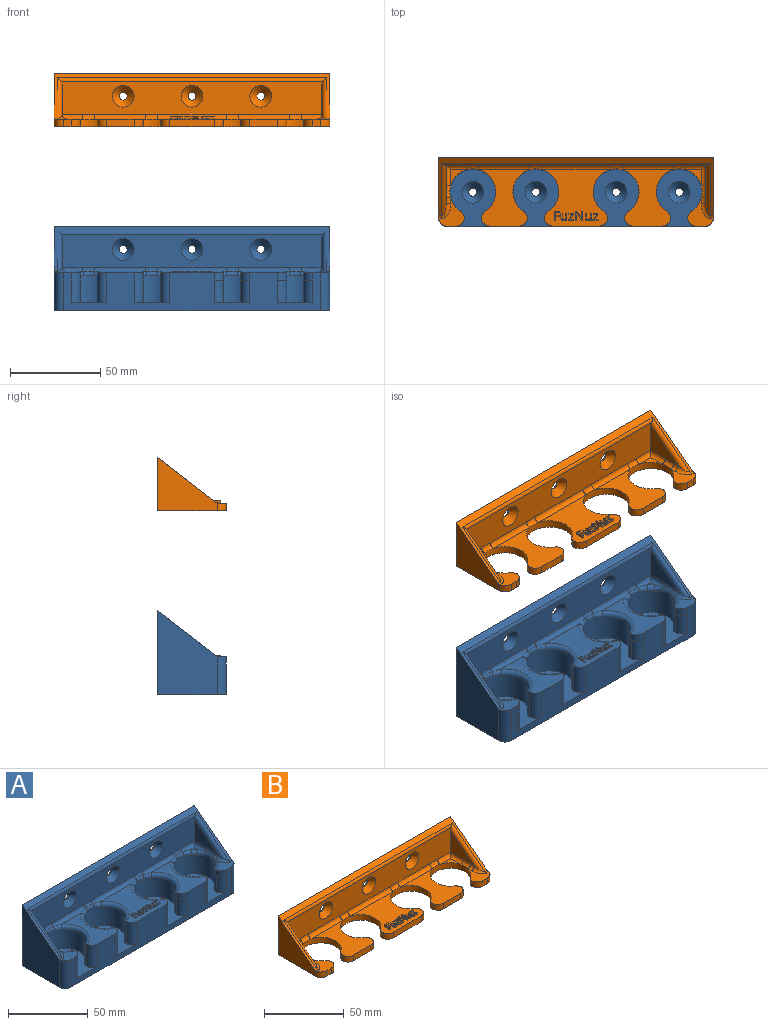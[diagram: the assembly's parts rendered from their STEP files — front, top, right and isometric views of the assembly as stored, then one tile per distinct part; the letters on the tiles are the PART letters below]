
ASSEMBLY  parts=2 mates=2
PART A: 201 faces, bbox 152.5x38.2x46.7 mm
  f0: plane 5.08x4.66mm, normal (0,0,1), area 0.3mm2, adj f20,f34,f35,f162
  f1: plane 5.08x4.66mm, normal (0,0,1), area 0.3mm2, adj f20,f36,f37,f161
  f2: plane 5.08x4.66mm, normal (0,0,1), area 0.3mm2, adj f20,f38,f39,f160
  f3: plane 5.08x4.66mm, normal (0,0,1), area 0.3mm2, adj f20,f22,f23,f159
  f4: plane 14.19x10.26mm, normal (0,0,1), area 76.6mm2, adj f20,f25,f27,f61,f62,f175
  f5: plane 14.19x10.26mm, normal (0,0,1), area 76.6mm2, adj f20,f22,f24,f50,f53,f163
  f6: plane 3.2x3.2mm, normal (0,0,1), area 4.6mm2, adj f44,f46,f170
  f7: plane 31.31x25.35mm, normal (0,0,1), area 350.7mm2, adj f20,f36,f39,f41,f167,f185
  f8: plane 34.88x31.31mm, normal (0,0,1), area 620.6mm2, adj f20,f32,f35,f45,f63,f64,f65,f66
  f9: plane 31.31x25.35mm, normal (0,0,1), area 350.7mm2, adj f20,f28,f31,f49,f173,f188
  f10: plane 46.61x33.02mm, normal (1,0,0), area 1119.7mm2, adj f15,f24,f40,f50,f154
  f11: plane 21.3x16.42mm, normal (1,0,0), area 174.6mm2, adj f12,f56,f58,f59,f60
  f12: plane 145.01x18.44mm, normal (0,-1,0), area 2298.1mm2, adj f11,f13,f41,f42,f43,f44,f45,f47
  f13: plane 21.3x16.42mm, normal (-1,0,0), area 174.6mm2, adj f12,f46,f48,f51,f55
  f14: cylinder r=12.7mm len=25.4mm, axis (0,0,-1), area 950.9mm2, adj f23,f38,f155,f163,f164,f165,f166,f167
  f15: plane 152.4x46.61mm, normal (0,1,0), area 7057.2mm2, adj f10,f16,f40,f148,f149,f150,f154
  f16: plane 46.61x33.02mm, normal (-1,0,0), area 1119.7mm2, adj f15,f25,f40,f62,f154
  f17: cylinder r=12.7mm len=25.4mm, axis (0,0,-1), area 950.9mm2, adj f26,f29,f158,f173,f174,f175,f176,f177
  f18: cylinder r=12.7mm len=25.4mm, axis (0,0,-1), area 943.3mm2, adj f30,f33,f157,f188,f189,f190,f191,f192
  f19: cylinder r=12.7mm len=25.4mm, axis (0,0,-1), area 943.3mm2, adj f34,f37,f156,f183,f184,f185,f186,f187
  f20: plane 142.24x21.21mm, normal (0,-1,0), area 1685.3mm2, adj f0,f1,f2,f3,f4,f5,f7,f8
  f21: plane 3.2x3.2mm, normal (0,0,1), area 4.6mm2, adj f54,f56,f180
  f22: cylinder r=5.08mm len=5.06mm, axis (0,0,-1), area 32.2mm2, adj f3,f5,f20,f23,f163
  f23: cylinder r=5.08mm len=16.95mm, axis (0,0,-1), area 78.6mm2, adj f3,f14,f22,f155,f159,f163
  f24: cylinder r=5.08mm len=21.36mm, axis (0,0,1), area 169.3mm2, adj f5,f10,f20,f50,f154
  f25: cylinder r=5.08mm len=21.36mm, axis (0,0,-1), area 169.3mm2, adj f4,f16,f20,f62,f154
  f26: cylinder r=5.08mm len=16.95mm, axis (0,0,-1), area 71.8mm2, adj f17,f27,f158,f175
  f27: cylinder r=5.08mm len=16.95mm, axis (0,0,-1), area 128.2mm2, adj f4,f20,f26,f158,f175
  f28: cylinder r=5.08mm len=16.95mm, axis (0,0,-1), area 128.2mm2, adj f9,f20,f29,f158,f173
  f29: cylinder r=5.08mm len=16.95mm, axis (0,0,-1), area 71.8mm2, adj f17,f28,f158,f173
  f30: cylinder r=5.08mm len=16.95mm, axis (0,0,-1), area 71.8mm2, adj f18,f31,f157,f188
  f31: cylinder r=5.08mm len=16.95mm, axis (0,0,-1), area 128.2mm2, adj f9,f20,f30,f157,f188
  f32: cylinder r=5.08mm len=16.95mm, axis (0,0,-1), area 128.2mm2, adj f8,f20,f33,f157,f190
  f33: cylinder r=5.08mm len=16.95mm, axis (0,0,-1), area 71.8mm2, adj f18,f32,f157,f190
  f34: cylinder r=5.08mm len=16.95mm, axis (0,0,-1), area 78.6mm2, adj f0,f19,f35,f156,f162,f183
  f35: cylinder r=5.08mm len=5.06mm, axis (0,0,-1), area 32.2mm2, adj f0,f8,f20,f34,f183
  f36: cylinder r=5.08mm len=5.06mm, axis (0,0,-1), area 32.2mm2, adj f1,f7,f20,f37,f185
  f37: cylinder r=5.08mm len=16.95mm, axis (0,0,-1), area 78.6mm2, adj f1,f19,f36,f156,f161,f185
  f38: cylinder r=5.08mm len=16.95mm, axis (0,0,-1), area 78.6mm2, adj f2,f14,f39,f155,f160,f167
  f39: cylinder r=5.08mm len=5.06mm, axis (0,0,-1), area 32.2mm2, adj f2,f7,f20,f38,f167
  f40: plane 152.4x32.34mm, normal (0,-0.61,0.79), area 753.2mm2, adj f10,f15,f16,f50,f55,f57,f59,f62
  f41: cylinder r=2.54mm len=28.26mm, axis (1,0,0), area 104.9mm2, adj f7,f12,f42,f43,f169,f187
  f42: bspline ~8.6x2.87mm, area 16.1mm2, adj f12,f41,f44,f171
  f43: bspline ~8.6x2.87mm, area 16.1mm2, adj f12,f41,f45,f186
  f44: cylinder r=2.54mm len=11.47mm, axis (1,0,0), area 36.7mm2, adj f6,f12,f42,f46,f172
  f45: cylinder r=2.54mm len=37.79mm, axis (1,0,0), area 142.9mm2, adj f8,f12,f43,f47,f184,f192
  f46: cylinder r=2.54mm len=11.47mm, axis (0,-1,0), area 36.7mm2, adj f6,f13,f44,f48,f168
  f47: bspline ~8.6x2.87mm, area 16.1mm2, adj f12,f45,f49,f191
  f48: bspline ~8.6x2.87mm, area 16.1mm2, adj f13,f46,f51,f166
  f49: cylinder r=2.54mm len=28.26mm, axis (1,0,0), area 104.9mm2, adj f9,f12,f47,f52,f174,f189
  f50: cylinder r=2.54mm len=1.71mm, axis (-1,0,0), area 2.8mm2, adj f5,f10,f24,f40,f53
  f51: cylinder r=2.54mm len=3.17mm, axis (0,-1,0), area 9.2mm2, adj f13,f48,f53,f165
  f52: bspline ~8.6x2.87mm, area 16.1mm2, adj f12,f49,f54,f176
  f53: bspline ~9.78x5.3mm, area 23.9mm2, adj f5,f50,f51,f55,f164
  f54: cylinder r=2.54mm len=11.47mm, axis (1,0,0), area 36.7mm2, adj f12,f21,f52,f56,f178
  f55: cylinder r=2.54mm len=30.62mm, axis (0,0.79,0.61), area 130.1mm2, adj f12,f13,f40,f53,f57
  f56: cylinder r=2.54mm len=11.47mm, axis (0,1,0), area 36.7mm2, adj f11,f21,f54,f58,f182
  f57: cylinder r=2.54mm len=148.97mm, axis (-1,0,0), area 341.6mm2, adj f12,f40,f55,f59
  f58: bspline ~8.6x2.87mm, area 16.1mm2, adj f11,f56,f60,f181
  f59: cylinder r=2.54mm len=30.62mm, axis (0,-0.79,-0.61), area 130.1mm2, adj f11,f12,f40,f57,f61
  f60: cylinder r=2.54mm len=3.17mm, axis (0,1,0), area 9.2mm2, adj f11,f58,f61,f179
  f61: bspline ~8.33x5.08mm, area 23.9mm2, adj f4,f59,f60,f62,f177
  f62: cylinder r=2.54mm len=1.71mm, axis (-1,0,0), area 2.8mm2, adj f4,f16,f25,f40,f61
  f63: plane 0.64x0.55mm, normal (0,-1,0), area 0.3mm2, adj f8,f64,f72,f73
  f64: plane 2.02x0.64mm, normal (1,0,0), area 1.3mm2, adj f8,f63,f65,f73
  f65: plane 1.96x0.64mm, normal (0,-1,0), area 1.2mm2, adj f8,f64,f66,f73
  f66: plane 0.64x0.49mm, normal (1,0,0), area 0.3mm2, adj f8,f65,f67,f73
  f67: plane 1.96x0.64mm, normal (0,1,0), area 1.2mm2, adj f8,f66,f68,f73
  f68: plane 1.73x0.64mm, normal (1,0,0), area 1.1mm2, adj f8,f67,f69,f73
  f69: plane 2.08x0.64mm, normal (0,-1,0), area 1.3mm2, adj f8,f68,f70,f73
  f70: plane 0.64x0.49mm, normal (1,0,0), area 0.3mm2, adj f8,f69,f71,f73
  f71: plane 2.63x0.64mm, normal (0,1,0), area 1.7mm2, adj f8,f70,f72,f73
  f72: plane 4.72x0.64mm, normal (-1,0,0), area 3mm2, adj f8,f63,f71,f73
  f73: plane 4.72x2.63mm, normal (0,0,1), area 4.6mm2, adj f63,f64,f65,f66,f67,f68,f69,f70
  f74: plane 2.3x0.64mm, normal (1,0,0), area 1.5mm2, adj f8,f75,f90,f91
  f75: plane 0.64x0.54mm, normal (0,1,0), area 0.3mm2, adj f8,f74,f76,f91
  f76: plane 2.31x0.64mm, normal (-1,0,0), area 1.5mm2, adj f8,f75,f77,f91
  f77: extruded ~0.98x0.64mm, area 0.7mm2, adj f8,f76,f78,f91
  f78: extruded ~0.97x0.64mm, area 0.7mm2, adj f8,f77,f79,f91
  f79: extruded ~0.67x0.64mm, area 0.4mm2, adj f8,f78,f80,f91
  f80: extruded ~0.64x0.46mm, area 0.4mm2, adj f8,f79,f81,f91
  f81: plane 0.64x0.03mm, normal (0,-1,0), area 0mm2, adj f8,f80,f82,f91
  f82: plane 0.64x0.47mm, normal (-0.99,-0.16,0), area 0.3mm2, adj f8,f81,f83,f91
  f83: plane 0.64x0.44mm, normal (0,-1,0), area 0.3mm2, adj f8,f82,f84,f91
  f84: plane 3.54x0.64mm, normal (1,0,0), area 2.2mm2, adj f8,f83,f85,f91
  f85: plane 0.64x0.54mm, normal (0,1,0), area 0.3mm2, adj f8,f84,f86,f91
  f86: plane 1.86x0.64mm, normal (-1,0,0), area 1.2mm2, adj f8,f85,f87,f91
  f87: extruded ~0.99x0.64mm, area 0.7mm2, adj f8,f86,f88,f91
  f88: extruded ~0.81x0.64mm, area 0.6mm2, adj f8,f87,f89,f91
  f89: extruded ~0.64x0.62mm, area 0.4mm2, adj f8,f88,f90,f91
  f90: extruded ~0.65x0.64mm, area 0.4mm2, adj f8,f74,f89,f91
  f91: plane 3.6x2.96mm, normal (0,0,1), area 4.6mm2, adj f74,f75,f76,f77,f78,f79,f80,f81
  f92: plane 2.57x0.64mm, normal (0,-1,0), area 1.6mm2, adj f8,f93,f101,f102
  f93: plane 0.64x0.42mm, normal (1,0,0), area 0.3mm2, adj f8,f92,f94,f102
  f94: plane 1.95x0.64mm, normal (0,1,0), area 1.2mm2, adj f8,f93,f95,f102
  f95: plane 2.71x1.9mm, normal (0.82,-0.58,0), area 2.1mm2, adj f8,f94,f96,f102
  f96: plane 0.64x0.42mm, normal (1,0,0), area 0.3mm2, adj f8,f95,f97,f102
  f97: plane 2.4x0.64mm, normal (0,1,0), area 1.5mm2, adj f8,f96,f98,f102
  f98: plane 0.64x0.42mm, normal (-1,0,0), area 0.3mm2, adj f8,f97,f99,f102
  f99: plane 1.81x0.64mm, normal (0,-1,0), area 1.1mm2, adj f8,f98,f100,f102
  f100: plane 2.76x1.93mm, normal (-0.82,0.57,0), area 2.1mm2, adj f8,f99,f101,f102
  f101: plane 0.64x0.36mm, normal (-1,0,0), area 0.2mm2, adj f8,f92,f100,f102
  f102: plane 3.54x2.57mm, normal (0,0,1), area 3.6mm2, adj f92,f93,f94,f95,f96,f97,f98,f99
  f103: plane 0.64x0.63mm, normal (0,-1,0), area 0.4mm2, adj f8,f104,f117,f118
  f104: plane 4.72x0.64mm, normal (1,0,0), area 3mm2, adj f8,f103,f105,f118
  f105: plane 0.64x0.51mm, normal (0,1,0), area 0.3mm2, adj f8,f104,f106,f118
  f106: plane 2.71x0.64mm, normal (-1,0,0), area 1.7mm2, adj f8,f105,f107,f118
  f107: extruded ~0.68x0.64mm, area 0.4mm2, adj f8,f106,f108,f118
  f108: extruded ~0.64x0.56mm, area 0.4mm2, adj f8,f107,f109,f118
  f109: plane 0.64x0.03mm, normal (0,1,0), area 0mm2, adj f8,f108,f110,f118
  f110: plane 3.94x2.57mm, normal (0.84,0.55,0), area 3mm2, adj f8,f109,f111,f118
  f111: plane 0.64x0.62mm, normal (0,1,0), area 0.4mm2, adj f8,f110,f112,f118
  f112: plane 4.72x0.64mm, normal (-1,0,0), area 3mm2, adj f8,f111,f113,f118
  f113: plane 0.64x0.51mm, normal (0,-1,0), area 0.3mm2, adj f8,f112,f114,f118
  f114: plane 2.68x0.64mm, normal (1,0,0), area 1.7mm2, adj f8,f113,f115,f118
  f115: extruded ~1.28x0.64mm, area 0.8mm2, adj f8,f114,f116,f118
  f116: plane 0.64x0.03mm, normal (0,-1,0), area 0mm2, adj f8,f115,f117,f118
  f117: plane 3.96x2.58mm, normal (-0.84,-0.55,0), area 3mm2, adj f8,f103,f116,f118
  f118: plane 4.72x3.69mm, normal (0,0,1), area 7.4mm2, adj f103,f104,f105,f106,f107,f108,f109,f110
  f119: plane 2.3x0.64mm, normal (1,0,0), area 1.5mm2, adj f8,f120,f135,f136
  f120: plane 0.64x0.54mm, normal (0,1,0), area 0.3mm2, adj f8,f119,f121,f136
  f121: plane 2.31x0.64mm, normal (-1,0,0), area 1.5mm2, adj f8,f120,f122,f136
  f122: extruded ~0.98x0.64mm, area 0.7mm2, adj f8,f121,f123,f136
  f123: extruded ~0.97x0.64mm, area 0.7mm2, adj f8,f122,f124,f136
  f124: extruded ~0.67x0.64mm, area 0.4mm2, adj f8,f123,f125,f136
  f125: extruded ~0.64x0.46mm, area 0.4mm2, adj f8,f124,f126,f136
  f126: plane 0.64x0.03mm, normal (0,-1,0), area 0mm2, adj f8,f125,f127,f136
  f127: plane 0.64x0.47mm, normal (-0.99,-0.16,0), area 0.3mm2, adj f8,f126,f128,f136
  f128: plane 0.64x0.44mm, normal (0,-1,0), area 0.3mm2, adj f8,f127,f129,f136
  f129: plane 3.54x0.64mm, normal (1,0,0), area 2.2mm2, adj f8,f128,f130,f136
  f130: plane 0.64x0.54mm, normal (0,1,0), area 0.3mm2, adj f8,f129,f131,f136
  f131: plane 1.86x0.64mm, normal (-1,0,0), area 1.2mm2, adj f8,f130,f132,f136
  f132: extruded ~0.99x0.64mm, area 0.7mm2, adj f8,f131,f133,f136
  f133: extruded ~0.81x0.64mm, area 0.6mm2, adj f8,f132,f134,f136
  f134: extruded ~0.64x0.62mm, area 0.4mm2, adj f8,f133,f135,f136
  f135: extruded ~0.65x0.64mm, area 0.4mm2, adj f8,f119,f134,f136
  f136: plane 3.6x2.96mm, normal (0,0,1), area 4.6mm2, adj f119,f120,f121,f122,f123,f124,f125,f126
  f137: plane 2.57x0.64mm, normal (0,-1,0), area 1.6mm2, adj f8,f138,f146,f147
  f138: plane 0.64x0.42mm, normal (1,0,0), area 0.3mm2, adj f8,f137,f139,f147
  f139: plane 1.95x0.64mm, normal (0,1,0), area 1.2mm2, adj f8,f138,f140,f147
  f140: plane 2.71x1.9mm, normal (0.82,-0.58,0), area 2.1mm2, adj f8,f139,f141,f147
  f141: plane 0.64x0.42mm, normal (1,0,0), area 0.3mm2, adj f8,f140,f142,f147
  f142: plane 2.4x0.64mm, normal (0,1,0), area 1.5mm2, adj f8,f141,f143,f147
  f143: plane 0.64x0.42mm, normal (-1,0,0), area 0.3mm2, adj f8,f142,f144,f147
  f144: plane 1.81x0.64mm, normal (0,-1,0), area 1.1mm2, adj f8,f143,f145,f147
  f145: plane 2.76x1.93mm, normal (-0.82,0.57,0), area 2.1mm2, adj f8,f144,f146,f147
  f146: plane 0.64x0.36mm, normal (-1,0,0), area 0.2mm2, adj f8,f137,f145,f147
  f147: plane 3.54x2.57mm, normal (0,0,1), area 3.6mm2, adj f137,f138,f139,f140,f141,f142,f143,f144
  f148: cylinder r=2.21mm len=4.42mm, axis (0,-1,0), area 6.2mm2, adj f15,f151
  f149: cylinder r=2.21mm len=4.42mm, axis (0,-1,0), area 6.2mm2, adj f15,f152
  f150: cylinder r=2.21mm len=4.42mm, axis (0,-1,0), area 6.2mm2, adj f15,f153
  f151: cone r=2.21mm half-angle=45deg, axis (0,-1,0), area 139.3mm2, adj f12,f148
  f152: cone r=2.21mm half-angle=45deg, axis (0,-1,0), area 139.3mm2, adj f12,f149
  f153: cone r=2.21mm half-angle=45deg, axis (0,-1,0), area 139.3mm2, adj f12,f150
  f154: plane 152.4x38.1mm, normal (0,0,-1), area 5734mm2, adj f10,f15,f16,f20,f24,f25,f193,f194
  f155: plane 31.75x25.4mm, normal (0,0,1), area 469.4mm2, adj f14,f20,f23,f38,f159,f160,f197
  f156: plane 31.75x25.4mm, normal (0,0,1), area 469.4mm2, adj f19,f20,f34,f37,f161,f162,f198
  f157: plane 31.75x25.4mm, normal (0,0,1), area 470.1mm2, adj f18,f20,f30,f31,f32,f33,f199
  f158: plane 31.75x25.4mm, normal (0,0,1), area 470.1mm2, adj f17,f20,f26,f27,f28,f29,f200
  f159: cylinder r=5.08mm len=12.7mm, axis (0,0,-1), area 90.7mm2, adj f3,f20,f23,f155
  f160: cylinder r=5.08mm len=12.7mm, axis (0,0,-1), area 90.7mm2, adj f2,f20,f38,f155
  f161: cylinder r=5.08mm len=12.7mm, axis (0,0,-1), area 90.7mm2, adj f1,f20,f37,f156
  f162: cylinder r=5.08mm len=12.7mm, axis (0,0,-1), area 90.7mm2, adj f0,f20,f34,f156
  f163: torus R=15.24mm, axis (0,0,1), area 28.9mm2, adj f5,f14,f22,f23,f164
  f164: bspline ~4.58x3.44mm, area 7.8mm2, adj f14,f53,f163,f165
  f165: bspline ~5.82x2.87mm, area 8.7mm2, adj f14,f51,f164,f166
  f166: bspline ~7.67x2.39mm, area 15.1mm2, adj f14,f48,f165,f168
  f167: torus R=15.24mm, axis (0,0,1), area 113.1mm2, adj f7,f14,f38,f39,f169
  f168: bspline ~8.84x4.39mm, area 17.6mm2, adj f14,f46,f166,f170
  f169: bspline ~8.84x4.39mm, area 17.6mm2, adj f14,f41,f167,f171
  f170: torus R=15.24mm, axis (0,0,1), area 16.2mm2, adj f6,f14,f168,f172
  f171: bspline ~7.67x2.39mm, area 15.1mm2, adj f14,f42,f169,f172
  f172: bspline ~8.84x4.39mm, area 17.6mm2, adj f14,f44,f170,f171
  f173: torus R=15.24mm, axis (0,0,1), area 113.1mm2, adj f9,f17,f28,f29,f174
  f174: bspline ~8.84x4.39mm, area 17.6mm2, adj f17,f49,f173,f176
  f175: torus R=15.24mm, axis (0,0,1), area 28.9mm2, adj f4,f17,f26,f27,f177
  f176: bspline ~7.67x2.39mm, area 15.1mm2, adj f17,f52,f174,f178
  f177: bspline ~4.73x3.4mm, area 7.8mm2, adj f17,f61,f175,f179
  f178: bspline ~8.84x4.39mm, area 17.6mm2, adj f17,f54,f176,f180
  f179: bspline ~5.51x2.83mm, area 8.7mm2, adj f17,f60,f177,f181
  f180: torus R=15.24mm, axis (0,0,1), area 16.2mm2, adj f17,f21,f178,f182
  f181: bspline ~7.67x2.39mm, area 15.1mm2, adj f17,f58,f179,f182
  f182: bspline ~8.84x4.39mm, area 17.6mm2, adj f17,f56,f180,f181
  f183: torus R=15.24mm, axis (0,0,1), area 113.1mm2, adj f8,f19,f34,f35,f184
  f184: bspline ~8.84x4.39mm, area 17.6mm2, adj f19,f45,f183,f186
  f185: torus R=15.24mm, axis (0,0,1), area 113.1mm2, adj f7,f19,f36,f37,f187
  f186: bspline ~7.67x2.39mm, area 15.1mm2, adj f19,f43,f184,f187
  f187: bspline ~8.84x4.39mm, area 17.6mm2, adj f19,f41,f185,f186
  f188: torus R=15.24mm, axis (0,0,1), area 113.1mm2, adj f9,f18,f30,f31,f189
  f189: bspline ~8.84x4.39mm, area 17.6mm2, adj f18,f49,f188,f191
  f190: torus R=15.24mm, axis (0,0,1), area 113.1mm2, adj f8,f18,f32,f33,f192
  f191: bspline ~7.67x2.39mm, area 15.1mm2, adj f18,f47,f189,f192
  f192: bspline ~8.84x4.39mm, area 17.6mm2, adj f18,f45,f190,f191
  f193: cylinder r=2.21mm len=4.42mm, axis (0,0,1), area 6.2mm2, adj f154,f200
  f194: cylinder r=2.21mm len=4.42mm, axis (0,0,1), area 6.2mm2, adj f154,f199
  f195: cylinder r=2.21mm len=4.42mm, axis (0,0,1), area 6.2mm2, adj f154,f198
  f196: cylinder r=2.21mm len=4.42mm, axis (0,0,1), area 6.2mm2, adj f154,f197
  f197: cone r=2.21mm half-angle=45deg, axis (0,0,1), area 139.3mm2, adj f155,f196
  f198: cone r=2.21mm half-angle=45deg, axis (0,0,1), area 139.3mm2, adj f156,f195
  f199: cone r=2.21mm half-angle=45deg, axis (0,0,1), area 139.3mm2, adj f157,f194
  f200: cone r=2.21mm half-angle=45deg, axis (0,0,1), area 139.3mm2, adj f158,f193
PART B: 155 faces, bbox 152.5x38.2x29.7 mm
  f0: plane 15.72x14.2mm, normal (0,0,1), area 101.4mm2, adj f14,f15,f26,f27,f28,f61,f62,f63
  f1: plane 15.72x14.2mm, normal (0,0,1), area 101.4mm2, adj f10,f11,f23,f24,f25,f51,f52,f54
  f2: plane 8.93x8.93mm, normal (0,0,1), area 25.5mm2, adj f10,f45,f47
  f3: plane 31.31x28.26mm, normal (0,0,1), area 511.4mm2, adj f10,f19,f20,f37,f38,f39,f40,f42
  f4: plane 37.79x31.31mm, normal (0,0,1), area 774.7mm2, adj f17,f18,f19,f33,f34,f35,f36,f46
  f5: plane 31.31x28.26mm, normal (0,0,1), area 511.4mm2, adj f15,f16,f17,f29,f30,f31,f32,f50
  f6: plane 33.02x29.65mm, normal (1,0,0), area 559.9mm2, adj f12,f22,f25,f41,f51
  f7: plane 21.3x16.42mm, normal (1,0,0), area 174.6mm2, adj f8,f57,f59,f60,f61
  f8: plane 145.01x18.44mm, normal (0,-1,0), area 2298.1mm2, adj f7,f9,f42,f43,f44,f45,f46,f48
  f9: plane 21.3x16.42mm, normal (-1,0,0), area 174.6mm2, adj f8,f47,f49,f52,f56
  f10: cylinder r=12.7mm len=25.4mm, axis (0,0,-1), area 276.1mm2, adj f1,f2,f3,f22,f24,f39,f43,f49
  f11: plane 4.25x4.13mm, normal (0,-1,0), area 17.6mm2, adj f1,f22,f23,f25
  f12: plane 152.4x29.65mm, normal (0,1,0), area 4473.3mm2, adj f6,f13,f22,f41,f149,f150,f151
  f13: plane 33.02x29.65mm, normal (-1,0,0), area 559.9mm2, adj f12,f22,f26,f41,f63
  f14: plane 4.25x4.13mm, normal (0,-1,0), area 17.6mm2, adj f0,f22,f26,f28
  f15: cylinder r=12.7mm len=25.4mm, axis (0,0,-1), area 276.1mm2, adj f0,f5,f21,f22,f27,f30,f53,f59
  f16: plane 15.24x4.25mm, normal (0,-1,0), area 64.8mm2, adj f5,f22,f29,f32
  f17: cylinder r=12.7mm len=25.4mm, axis (0,0,-1), area 276.1mm2, adj f4,f5,f22,f31,f34,f48
  f18: plane 24.77x4.25mm, normal (0,-1,0), area 105.4mm2, adj f4,f22,f33,f36
  f19: cylinder r=12.7mm len=25.4mm, axis (0,0,-1), area 276.1mm2, adj f3,f4,f22,f35,f38,f44
  f20: plane 15.24x4.25mm, normal (0,-1,0), area 64.8mm2, adj f3,f22,f37,f40
  f21: plane 8.93x8.93mm, normal (0,0,1), area 25.5mm2, adj f15,f55,f57
  f22: plane 152.4x38.1mm, normal (0,0,-1), area 3459.7mm2, adj f6,f10,f11,f12,f13,f14,f15,f16
  f23: cylinder r=5.08mm len=5.06mm, axis (0,0,-1), area 32.2mm2, adj f1,f11,f22,f24
  f24: cylinder r=5.08mm len=4.25mm, axis (0,0,-1), area 19.5mm2, adj f1,f10,f22,f23
  f25: cylinder r=5.08mm len=5.08mm, axis (0,0,1), area 34mm2, adj f1,f6,f11,f22,f51
  f26: cylinder r=5.08mm len=5.08mm, axis (0,0,-1), area 34mm2, adj f0,f13,f14,f22,f63
  f27: cylinder r=5.08mm len=4.25mm, axis (0,0,-1), area 19.5mm2, adj f0,f15,f22,f28
  f28: cylinder r=5.08mm len=5.06mm, axis (0,0,-1), area 32.2mm2, adj f0,f14,f22,f27
  f29: cylinder r=5.08mm len=5.06mm, axis (0,0,-1), area 32.2mm2, adj f5,f16,f22,f30
  f30: cylinder r=5.08mm len=4.25mm, axis (0,0,-1), area 19.5mm2, adj f5,f15,f22,f29
  f31: cylinder r=5.08mm len=4.25mm, axis (0,0,-1), area 19.5mm2, adj f5,f17,f22,f32
  f32: cylinder r=5.08mm len=5.06mm, axis (0,0,-1), area 32.2mm2, adj f5,f16,f22,f31
  f33: cylinder r=5.08mm len=5.06mm, axis (0,0,-1), area 32.2mm2, adj f4,f18,f22,f34
  f34: cylinder r=5.08mm len=4.25mm, axis (0,0,-1), area 19.5mm2, adj f4,f17,f22,f33
  f35: cylinder r=5.08mm len=4.25mm, axis (0,0,-1), area 19.5mm2, adj f4,f19,f22,f36
  f36: cylinder r=5.08mm len=5.06mm, axis (0,0,-1), area 32.2mm2, adj f4,f18,f22,f35
  f37: cylinder r=5.08mm len=5.06mm, axis (0,0,-1), area 32.2mm2, adj f3,f20,f22,f38
  f38: cylinder r=5.08mm len=4.25mm, axis (0,0,-1), area 19.5mm2, adj f3,f19,f22,f37
  f39: cylinder r=5.08mm len=4.25mm, axis (0,0,-1), area 19.5mm2, adj f3,f10,f22,f40
  f40: cylinder r=5.08mm len=5.06mm, axis (0,0,-1), area 32.2mm2, adj f3,f20,f22,f39
  f41: plane 152.4x32.34mm, normal (0,-0.61,0.79), area 753.2mm2, adj f6,f12,f13,f51,f56,f58,f60,f63
  f42: cylinder r=2.54mm len=28.26mm, axis (1,0,0), area 112.8mm2, adj f3,f8,f43,f44
  f43: bspline ~8.6x2.87mm, area 24.6mm2, adj f8,f10,f42,f45
  f44: bspline ~8.6x2.87mm, area 24.6mm2, adj f8,f19,f42,f46
  f45: cylinder r=2.54mm len=11.47mm, axis (1,0,0), area 42.1mm2, adj f2,f8,f43,f47
  f46: cylinder r=2.54mm len=37.79mm, axis (1,0,0), area 150.8mm2, adj f4,f8,f44,f48
  f47: cylinder r=2.54mm len=11.47mm, axis (0,-1,0), area 42.1mm2, adj f2,f9,f45,f49
  f48: bspline ~8.6x2.87mm, area 24.6mm2, adj f8,f17,f46,f50
  f49: bspline ~8.6x2.87mm, area 24.6mm2, adj f9,f10,f47,f52
  f50: cylinder r=2.54mm len=28.26mm, axis (1,0,0), area 112.8mm2, adj f5,f8,f48,f53
  f51: cylinder r=2.54mm len=1.71mm, axis (-1,0,0), area 2.8mm2, adj f1,f6,f25,f41,f54
  f52: cylinder r=2.54mm len=3.17mm, axis (0,-1,0), area 12.7mm2, adj f1,f9,f49,f54
  f53: bspline ~8.6x2.87mm, area 24.6mm2, adj f8,f15,f50,f55
  f54: bspline ~8.33x5.08mm, area 24.7mm2, adj f1,f51,f52,f56
  f55: cylinder r=2.54mm len=11.47mm, axis (1,0,0), area 42.1mm2, adj f8,f21,f53,f57
  f56: cylinder r=2.54mm len=30.62mm, axis (0,0.79,0.61), area 130.1mm2, adj f8,f9,f41,f54,f58
  f57: cylinder r=2.54mm len=11.47mm, axis (0,1,0), area 42.1mm2, adj f7,f21,f55,f59
  f58: cylinder r=2.54mm len=148.97mm, axis (-1,0,0), area 341.6mm2, adj f8,f41,f56,f60
  f59: bspline ~8.6x2.87mm, area 24.6mm2, adj f7,f15,f57,f61
  f60: cylinder r=2.54mm len=30.62mm, axis (0,-0.79,-0.61), area 130.1mm2, adj f7,f8,f41,f58,f62
  f61: cylinder r=2.54mm len=3.17mm, axis (0,1,0), area 12.7mm2, adj f0,f7,f59,f62
  f62: bspline ~8.33x5.08mm, area 24.7mm2, adj f0,f60,f61,f63
  f63: cylinder r=2.54mm len=1.71mm, axis (-1,0,0), area 2.8mm2, adj f0,f13,f26,f41,f62
  f64: plane 1.27x0.61mm, normal (0,-1,0), area 0.8mm2, adj f4,f65,f73,f74
  f65: plane 2.24x1.27mm, normal (1,0,0), area 2.8mm2, adj f4,f64,f66,f74
  f66: plane 2.17x1.27mm, normal (0,-1,0), area 2.8mm2, adj f4,f65,f67,f74
  f67: plane 1.27x0.54mm, normal (1,0,0), area 0.7mm2, adj f4,f66,f68,f74
  f68: plane 2.17x1.27mm, normal (0,1,0), area 2.8mm2, adj f4,f67,f69,f74
  f69: plane 1.92x1.27mm, normal (1,0,0), area 2.4mm2, adj f4,f68,f70,f74
  f70: plane 2.31x1.27mm, normal (0,-1,0), area 2.9mm2, adj f4,f69,f71,f74
  f71: plane 1.27x0.54mm, normal (1,0,0), area 0.7mm2, adj f4,f70,f72,f74
  f72: plane 2.92x1.27mm, normal (0,1,0), area 3.7mm2, adj f4,f71,f73,f74
  f73: plane 5.24x1.27mm, normal (-1,0,0), area 6.7mm2, adj f4,f64,f72,f74
  f74: plane 5.24x2.92mm, normal (0,0,1), area 5.6mm2, adj f64,f65,f66,f67,f68,f69,f70,f71
  f75: plane 2.55x1.27mm, normal (1,0,0), area 3.2mm2, adj f4,f76,f91,f92
  f76: plane 1.27x0.6mm, normal (0,1,0), area 0.8mm2, adj f4,f75,f77,f92
  f77: plane 2.57x1.27mm, normal (-1,0,0), area 3.3mm2, adj f4,f76,f78,f92
  f78: extruded ~1.27x1.09mm, area 1.5mm2, adj f4,f77,f79,f92
  f79: extruded ~1.27x1.07mm, area 1.5mm2, adj f4,f78,f80,f92
  f80: extruded ~1.27x0.74mm, area 1mm2, adj f4,f79,f81,f92
  f81: extruded ~1.27x0.51mm, area 0.9mm2, adj f4,f80,f82,f92
  f82: plane 1.27x0.03mm, normal (0,-1,0), area 0mm2, adj f4,f81,f83,f92
  f83: plane 1.27x0.53mm, normal (-0.99,-0.16,0), area 0.7mm2, adj f4,f82,f84,f92
  f84: plane 1.27x0.49mm, normal (0,-1,0), area 0.6mm2, adj f4,f83,f85,f92
  f85: plane 3.93x1.27mm, normal (1,0,0), area 5mm2, adj f4,f84,f86,f92
  f86: plane 1.27x0.6mm, normal (0,1,0), area 0.8mm2, adj f4,f85,f87,f92
  f87: plane 2.07x1.27mm, normal (-1,0,0), area 2.6mm2, adj f4,f86,f88,f92
  f88: extruded ~1.27x1.1mm, area 1.5mm2, adj f4,f87,f89,f92
  f89: extruded ~1.27x0.9mm, area 1.3mm2, adj f4,f88,f90,f92
  f90: extruded ~1.27x0.68mm, area 0.9mm2, adj f4,f89,f91,f92
  f91: extruded ~1.27x0.72mm, area 1mm2, adj f4,f75,f90,f92
  f92: plane 4x3.29mm, normal (0,0,1), area 5.6mm2, adj f75,f76,f77,f78,f79,f80,f81,f82
  f93: plane 2.85x1.27mm, normal (0,-1,0), area 3.6mm2, adj f4,f94,f102,f103
  f94: plane 1.27x0.46mm, normal (1,0,0), area 0.6mm2, adj f4,f93,f95,f103
  f95: plane 2.17x1.27mm, normal (0,1,0), area 2.8mm2, adj f4,f94,f96,f103
  f96: plane 3.01x2.12mm, normal (0.82,-0.58,0), area 4.7mm2, adj f4,f95,f97,f103
  f97: plane 1.27x0.46mm, normal (1,0,0), area 0.6mm2, adj f4,f96,f98,f103
  f98: plane 2.66x1.27mm, normal (0,1,0), area 3.4mm2, adj f4,f97,f99,f103
  f99: plane 1.27x0.46mm, normal (-1,0,0), area 0.6mm2, adj f4,f98,f100,f103
  f100: plane 2.01x1.27mm, normal (0,-1,0), area 2.6mm2, adj f4,f99,f101,f103
  f101: plane 3.06x2.14mm, normal (-0.82,0.57,0), area 4.7mm2, adj f4,f100,f102,f103
  f102: plane 1.27x0.41mm, normal (-1,0,0), area 0.5mm2, adj f4,f93,f101,f103
  f103: plane 3.93x2.85mm, normal (0,0,1), area 4.5mm2, adj f93,f94,f95,f96,f97,f98,f99,f100
  f104: plane 1.27x0.7mm, normal (0,-1,0), area 0.9mm2, adj f4,f105,f118,f119
  f105: plane 5.24x1.27mm, normal (1,0,0), area 6.7mm2, adj f4,f104,f106,f119
  f106: plane 1.27x0.57mm, normal (0,1,0), area 0.7mm2, adj f4,f105,f107,f119
  f107: plane 3.01x1.27mm, normal (-1,0,0), area 3.8mm2, adj f4,f106,f108,f119
  f108: extruded ~1.27x0.75mm, area 1mm2, adj f4,f107,f109,f119
  f109: extruded ~1.27x0.62mm, area 0.8mm2, adj f4,f108,f110,f119
  f110: plane 1.27x0.03mm, normal (0,1,0), area 0mm2, adj f4,f109,f111,f119
  f111: plane 4.38x2.86mm, normal (0.84,0.55,0), area 6.6mm2, adj f4,f110,f112,f119
  f112: plane 1.27x0.69mm, normal (0,1,0), area 0.9mm2, adj f4,f111,f113,f119
  f113: plane 5.24x1.27mm, normal (-1,0,0), area 6.7mm2, adj f4,f112,f114,f119
  f114: plane 1.27x0.56mm, normal (0,-1,0), area 0.7mm2, adj f4,f113,f115,f119
  f115: plane 2.98x1.27mm, normal (1,0,0), area 3.8mm2, adj f4,f114,f116,f119
  f116: extruded ~1.42x1.27mm, area 1.8mm2, adj f4,f115,f117,f119
  f117: plane 1.27x0.03mm, normal (0,-1,0), area 0mm2, adj f4,f116,f118,f119
  f118: plane 4.4x2.87mm, normal (-0.84,-0.55,0), area 6.7mm2, adj f4,f104,f117,f119
  f119: plane 5.24x4.1mm, normal (0,0,1), area 9.1mm2, adj f104,f105,f106,f107,f108,f109,f110,f111
  f120: plane 2.55x1.27mm, normal (1,0,0), area 3.2mm2, adj f4,f121,f136,f137
  f121: plane 1.27x0.6mm, normal (0,1,0), area 0.8mm2, adj f4,f120,f122,f137
  f122: plane 2.57x1.27mm, normal (-1,0,0), area 3.3mm2, adj f4,f121,f123,f137
  f123: extruded ~1.27x1.09mm, area 1.5mm2, adj f4,f122,f124,f137
  f124: extruded ~1.27x1.07mm, area 1.5mm2, adj f4,f123,f125,f137
  f125: extruded ~1.27x0.74mm, area 1mm2, adj f4,f124,f126,f137
  f126: extruded ~1.27x0.51mm, area 0.9mm2, adj f4,f125,f127,f137
  f127: plane 1.27x0.03mm, normal (0,-1,0), area 0mm2, adj f4,f126,f128,f137
  f128: plane 1.27x0.53mm, normal (-0.99,-0.16,0), area 0.7mm2, adj f4,f127,f129,f137
  f129: plane 1.27x0.49mm, normal (0,-1,0), area 0.6mm2, adj f4,f128,f130,f137
  f130: plane 3.93x1.27mm, normal (1,0,0), area 5mm2, adj f4,f129,f131,f137
  f131: plane 1.27x0.6mm, normal (0,1,0), area 0.8mm2, adj f4,f130,f132,f137
  f132: plane 2.07x1.27mm, normal (-1,0,0), area 2.6mm2, adj f4,f131,f133,f137
  f133: extruded ~1.27x1.1mm, area 1.5mm2, adj f4,f132,f134,f137
  f134: extruded ~1.27x0.9mm, area 1.3mm2, adj f4,f133,f135,f137
  f135: extruded ~1.27x0.68mm, area 0.9mm2, adj f4,f134,f136,f137
  f136: extruded ~1.27x0.72mm, area 1mm2, adj f4,f120,f135,f137
  f137: plane 4x3.29mm, normal (0,0,1), area 5.6mm2, adj f120,f121,f122,f123,f124,f125,f126,f127
  f138: plane 2.85x1.27mm, normal (0,-1,0), area 3.6mm2, adj f4,f139,f147,f148
  f139: plane 1.27x0.46mm, normal (1,0,0), area 0.6mm2, adj f4,f138,f140,f148
  f140: plane 2.17x1.27mm, normal (0,1,0), area 2.8mm2, adj f4,f139,f141,f148
  f141: plane 3.01x2.12mm, normal (0.82,-0.58,0), area 4.7mm2, adj f4,f140,f142,f148
  f142: plane 1.27x0.46mm, normal (1,0,0), area 0.6mm2, adj f4,f141,f143,f148
  f143: plane 2.66x1.27mm, normal (0,1,0), area 3.4mm2, adj f4,f142,f144,f148
  f144: plane 1.27x0.46mm, normal (-1,0,0), area 0.6mm2, adj f4,f143,f145,f148
  f145: plane 2.01x1.27mm, normal (0,-1,0), area 2.6mm2, adj f4,f144,f146,f148
  f146: plane 3.06x2.14mm, normal (-0.82,0.57,0), area 4.7mm2, adj f4,f145,f147,f148
  f147: plane 1.27x0.41mm, normal (-1,0,0), area 0.5mm2, adj f4,f138,f146,f148
  f148: plane 3.93x2.85mm, normal (0,0,1), area 4.5mm2, adj f138,f139,f140,f141,f142,f143,f144,f145
  f149: cylinder r=2.21mm len=4.42mm, axis (0,-1,0), area 6.2mm2, adj f12,f152
  f150: cylinder r=2.21mm len=4.42mm, axis (0,-1,0), area 6.2mm2, adj f12,f153
  f151: cylinder r=2.21mm len=4.42mm, axis (0,-1,0), area 6.2mm2, adj f12,f154
  f152: cone r=2.21mm half-angle=45deg, axis (0,-1,0), area 139.3mm2, adj f8,f149
  f153: cone r=2.21mm half-angle=45deg, axis (0,-1,0), area 139.3mm2, adj f8,f150
  f154: cone r=2.21mm half-angle=45deg, axis (0,-1,0), area 139.3mm2, adj f8,f151
PLACE A t=(24,-44.92,-232.69)mm
PLACE B t=(24,-44.92,-147.89)mm
MATE planar B.f12 <-> A.f15  axis (0,1,0) through (24,-25.87,-133.08)mm
MATE planar B.f6 <-> A.f10  axis (1,0,0) through (100.2,-38.26,-137.83)mm
